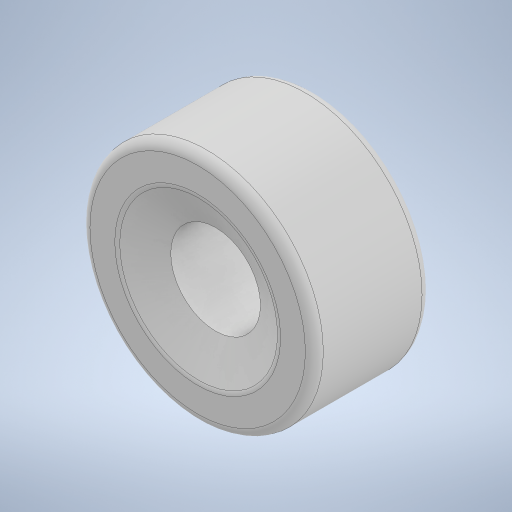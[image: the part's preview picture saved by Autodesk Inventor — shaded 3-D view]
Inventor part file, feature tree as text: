
AUTODESK INVENTOR PART (.ipt)
format: ipt  version: 2023 (Build 270158000, 158)  size: 274,944 bytes
history: native  units: in
note: dims shown in document units (in); Inventor stores cm internally (conversion verified against a paired STEP export)
features: sketch x3, extrude x1, hole x1, revolve x1, plane x1, mirror x1, fillet x1
ambient origin geometry x8: Origin, YZ Plane, XZ Plane, XY Plane, X Axis, Y Axis, Z Axis, Center Point
bodies: Solid1 (feature_tree)
feature tree (9):
  extrude  "Extrusion1"  Depth=0.5118in TaperAngle=0.0deg
  hole  "Hole1"  [1 undecoded]
  revolve  "Revolution1"  Angle=90.0deg
  plane  "Work Plane1"
  mirror  "Mirror1"
  fillet  "Fillet1"  Radius=0.0394in
  sketch  "Sketch1"  dims[d0=1.0236in d1=0.5118in d2=0.0in]
  sketch  "Sketch2"  dims[d3=0.3937in d4=0.2362in d5=0.1575in d6=0.0787in d7=90.0deg d8=0.315in d9=0.8108in d10=0.0787in]
  sketch  "Sketch3"  dims[d11=0.1575in d12=90.0deg d13=0.0394in d14=0.0in d15=0.0in d16=0.0in]
note: 1 required parameter value undecoded (feature->parameter linkage not recoverable at this tier; creation-order binding heuristic only, values carry confidence <= 0.55)
